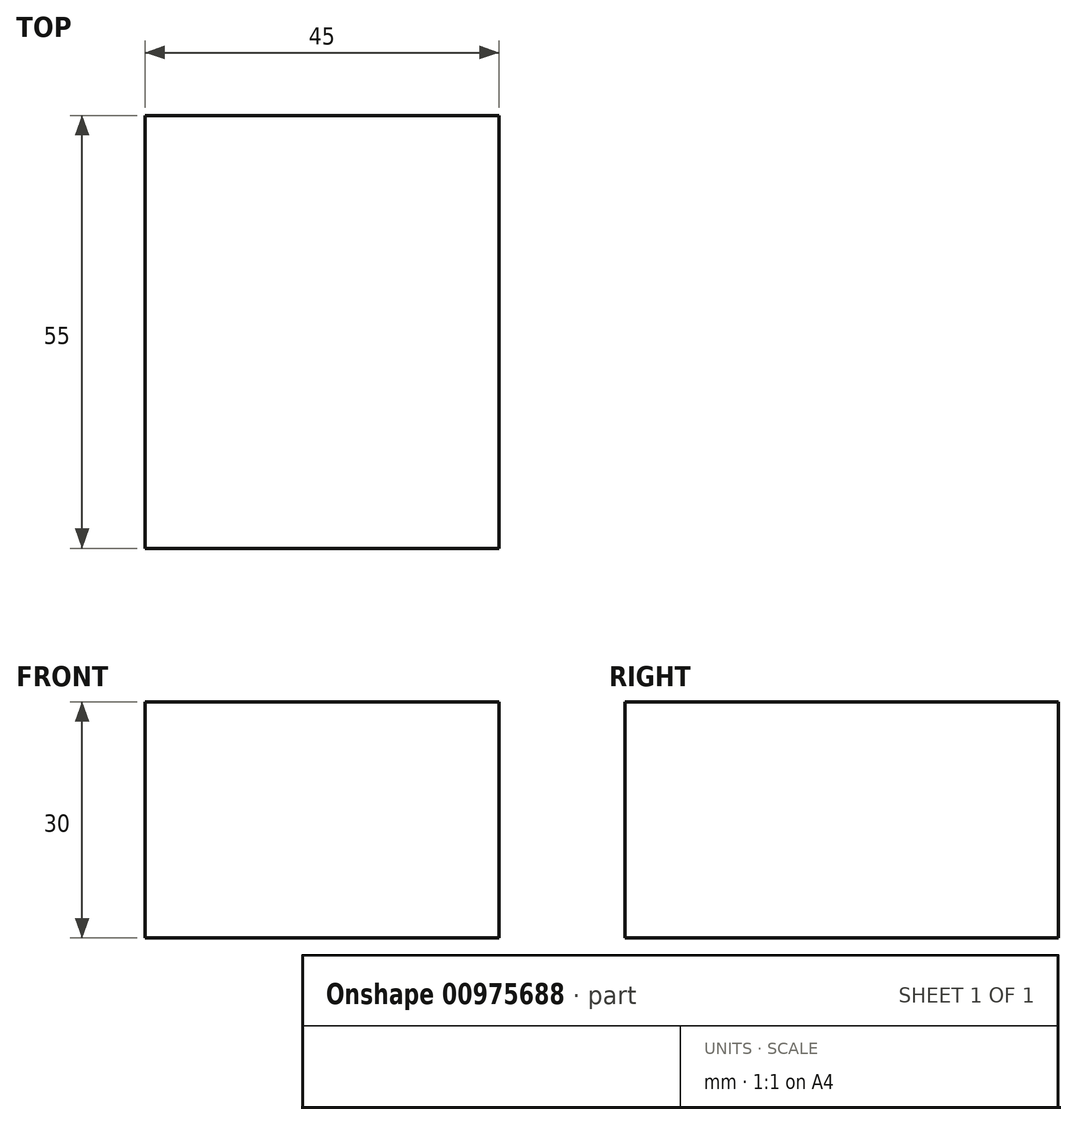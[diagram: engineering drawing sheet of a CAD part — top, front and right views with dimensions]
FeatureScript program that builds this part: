
annotation { "Feature Type Name" : "Feature", "Feature Type Description" : "" }
export const myFeature = defineFeature(function(context is Context, id is Id, definition is map)
    precondition{}
    {
        {
            var Q0;
            Q0=qCreatedBy(makeId("Top.planeOp"),FACE);
            var sketch = newSketch(context, id + "F0", { "sketchPlane" : qUnion([Q0])});
            skLineSegment(sketch, "E0.bottom", {"start": v(22.5, -27.5) * mm, "end": v(-22.5, -27.5) * mm});
            skLineSegment(sketch, "E0.top", {"start": v(22.5, 27.5) * mm, "end": v(-22.5, 27.5) * mm});
            skLineSegment(sketch, "E0.left", {"start": v(22.5, -27.5) * mm, "end": v(22.5, 27.5) * mm});
            skLineSegment(sketch, "E0.right", {"start": v(-22.5, -27.5) * mm, "end": v(-22.5, 27.5) * mm});
            skPoint(sketch, "E0.middle", {"position": v(0, 0) * mm});
            skSolve(sketch);
        }
        {
            var Q0;
            Q0 = qSketchRegion(id + "F0", true);
            extrude(context, id + "F1", {"entities" : qUnion([Q0]), "depth" : 30 * mm, "offsetDistance" : 25 * mm});
        }
    });
